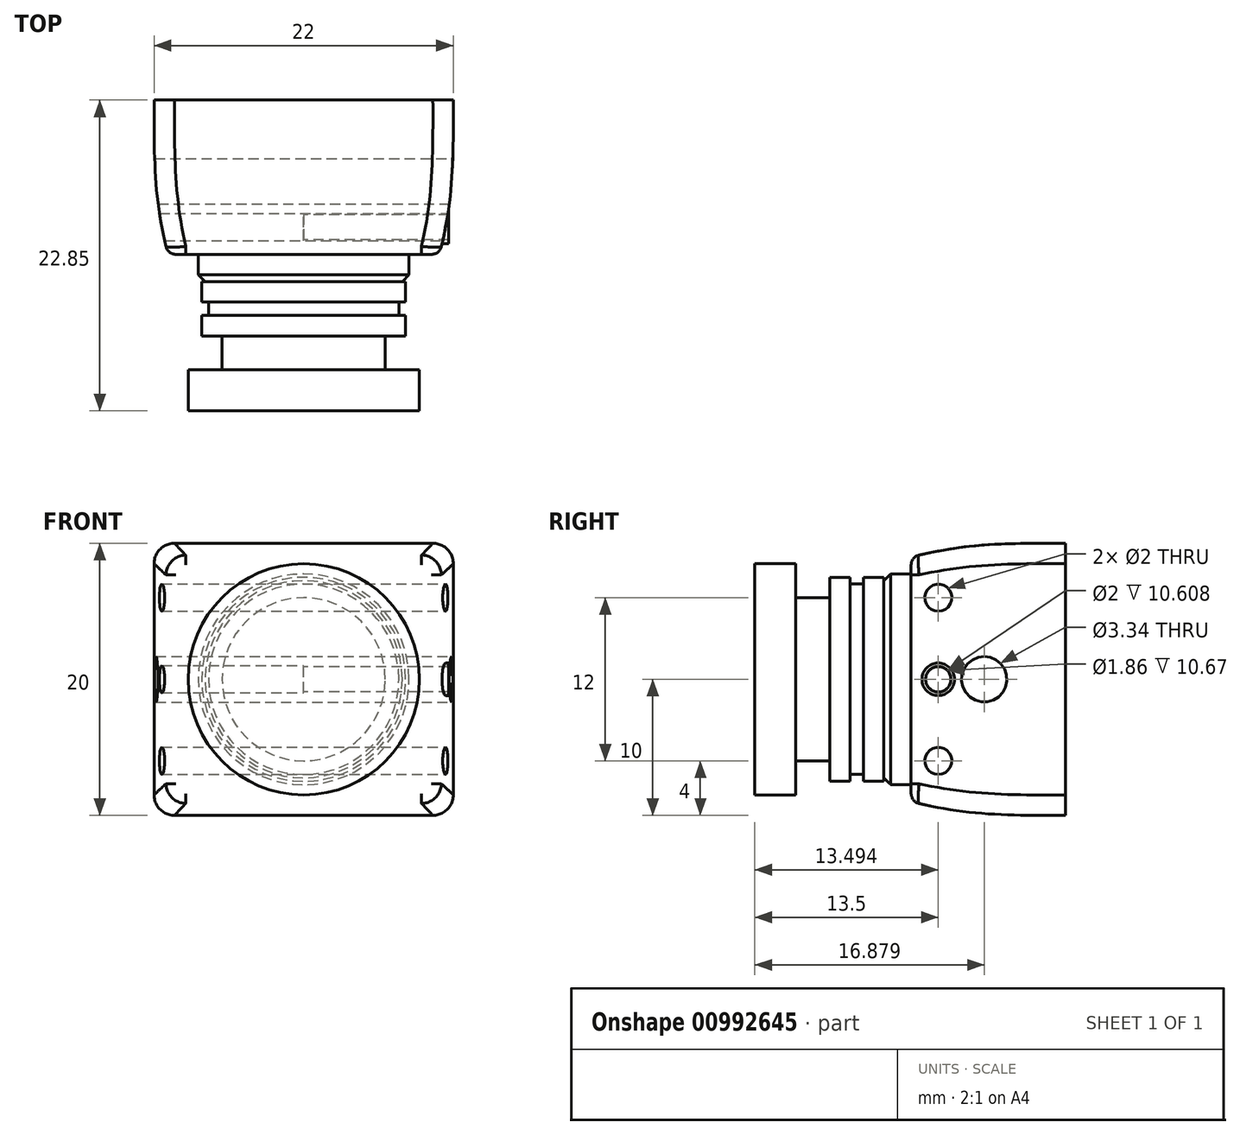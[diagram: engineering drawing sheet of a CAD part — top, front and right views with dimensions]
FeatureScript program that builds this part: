
annotation { "Feature Type Name" : "Feature", "Feature Type Description" : "" }
export const myFeature = defineFeature(function(context is Context, id is Id, definition is map)
    precondition{}
    {
        {
            var Q0;
            Q0=qCreatedBy(makeId("Front.planeOp"),FACE);
            var sketch = newSketch(context, id + "F0", { "sketchPlane" : qUnion([Q0])});
            skLineSegment(sketch, "E0.bottom", {"start": v(11, -10) * mm, "end": v(-11, -10) * mm});
            skLineSegment(sketch, "E0.top", {"start": v(11, 10) * mm, "end": v(-11, 10) * mm});
            skLineSegment(sketch, "E0.left", {"start": v(11, -10) * mm, "end": v(11, 10) * mm});
            skLineSegment(sketch, "E0.right", {"start": v(-11, -10) * mm, "end": v(-11, 10) * mm});
            skPoint(sketch, "E0.middle", {"position": v(0, 0) * mm});
            skSolve(sketch);
        }
        {
            var Q0;
            Q0=qCreatedBy(makeId("Front.planeOp"),FACE);
            cPlane(context, id + "F1", {"entities" : qUnion([Q0]), "cplaneType" : CPlaneType.OFFSET, "offset" : 11.35 * mm, "width" : 150 * mm, "height" : 150 * mm});
        }
        {
            var Q0;
            Q0=qCreatedBy(id+"F1.planeOp",FACE);
            var sketch = newSketch(context, id + "F2", { "sketchPlane" : qUnion([Q0])});
            skLineSegment(sketch, "E1.bottom", {"start": v(10, -9) * mm, "end": v(-10, -9) * mm});
            skLineSegment(sketch, "E1.top", {"start": v(10, 9) * mm, "end": v(-10, 9) * mm});
            skLineSegment(sketch, "E1.left", {"start": v(10, -9) * mm, "end": v(10, 9) * mm});
            skLineSegment(sketch, "E1.right", {"start": v(-10, -9) * mm, "end": v(-10, 9) * mm});
            skPoint(sketch, "E1.middle", {"position": v(0, 0) * mm});
            skSolve(sketch);
        }
        {
            var Q0;
            Q0=qCreatedBy(makeId("Front.planeOp"),FACE);
            cPlane(context, id + "F3", {"entities" : qUnion([Q0]), "cplaneType" : CPlaneType.OFFSET, "offset" : 9 * mm, "width" : 150 * mm, "height" : 150 * mm});
        }
        {
            var Q0;
            Q0=qCreatedBy(id+"F3.planeOp",FACE);
            var sketch = newSketch(context, id + "F4", { "sketchPlane" : qUnion([Q0])});
            skLineSegment(sketch, "E2.bottom", {"start": v(10.5, -9.5) * mm, "end": v(-10.5, -9.5) * mm});
            skLineSegment(sketch, "E2.top", {"start": v(10.5, 9.5) * mm, "end": v(-10.5, 9.5) * mm});
            skLineSegment(sketch, "E2.left", {"start": v(10.5, -9.5) * mm, "end": v(10.5, 9.5) * mm});
            skLineSegment(sketch, "E2.right", {"start": v(-10.5, -9.5) * mm, "end": v(-10.5, 9.5) * mm});
            skPoint(sketch, "E2.middle", {"position": v(0, 0) * mm});
            skSolve(sketch);
        }
        {
            var Q0;
            Q0=qSketchRegion(id+"F0",true);
            var Q1;
            Q1=qSketchRegion(id+"F4",true);
            var Q2;
            Q2=qSketchRegion(id+"F2",true);
            loft(context, id + "F5", {"sheetProfilesArray" : [{ "sheetProfileEntities" : qUnion([Q0]) }, { "sheetProfileEntities" : qUnion([Q1]) }, { "sheetProfileEntities" : qUnion([Q2]) }]});
        }
        {
            var Q0;
            Q0=makeQuery(id+"F5.opLoft","SWEPT_EDGE",EDGE,{"disambiguationData":[OSD([sQuery(id+"F0.wireOp",EDGE,"E0.top"),sQuery(id+"F0.wireOp",EDGE,"E0.left"),sQuery(id+"F2.wireOp",EDGE,"E1.top"),sQuery(id+"F2.wireOp",EDGE,"E1.left"),sQuery(id+"F4.wireOp",EDGE,"E2.top"),sQuery(id+"F4.wireOp",EDGE,"E2.left")])]});
            var Q1;
            Q1=makeQuery(id+"F5.opLoft","SWEPT_EDGE",EDGE,{"disambiguationData":[OSD([sQuery(id+"F0.wireOp",EDGE,"E0.top"),sQuery(id+"F0.wireOp",EDGE,"E0.right"),sQuery(id+"F2.wireOp",EDGE,"E1.top"),sQuery(id+"F2.wireOp",EDGE,"E1.right"),sQuery(id+"F4.wireOp",EDGE,"E2.top"),sQuery(id+"F4.wireOp",EDGE,"E2.right")])]});
            var Q2;
            Q2=makeQuery(id+"F5.opLoft","SWEPT_EDGE",EDGE,{"disambiguationData":[OSD([sQuery(id+"F0.wireOp",EDGE,"E0.bottom"),sQuery(id+"F0.wireOp",EDGE,"E0.right"),sQuery(id+"F2.wireOp",EDGE,"E1.bottom"),sQuery(id+"F2.wireOp",EDGE,"E1.right"),sQuery(id+"F4.wireOp",EDGE,"E2.bottom"),sQuery(id+"F4.wireOp",EDGE,"E2.right")])]});
            var Q3;
            Q3=makeQuery(id+"F5.opLoft","SWEPT_EDGE",EDGE,{"disambiguationData":[OSD([sQuery(id+"F0.wireOp",EDGE,"E0.bottom"),sQuery(id+"F0.wireOp",EDGE,"E0.left"),sQuery(id+"F2.wireOp",EDGE,"E1.bottom"),sQuery(id+"F2.wireOp",EDGE,"E1.left"),sQuery(id+"F4.wireOp",EDGE,"E2.bottom"),sQuery(id+"F4.wireOp",EDGE,"E2.left")])]});
            fillet(context, id + "F6", {"entities" : qUnion([Q0, Q1, Q2, Q3]), "radius" : 1.5 * mm, "tangentPropagation" : true, "allowEdgeOverflow" : false});
        }
        {
            var Q0;
            Q0=makeQuery(id+"F5.opLoft","MID_CAP_EDGE",EDGE,{"disambiguationData":[OSD([sQuery(id+"F2.wireOp",EDGE,"E1.top"),sQuery(id+"F2.wireOp",EDGE,"E1.left"),sQuery(id+"F2.wireOp",EDGE,"E1.right")])],"capPos":2.0});
            fillet(context, id + "F7", {"entities" : qUnion([Q0]), "radius" : 0.75 * mm, "tangentPropagation" : true, "allowEdgeOverflow" : false});
        }
        {
            var Q0;
            Q0=makeQuery(id+"F5.opLoft","CAP_FACE",FACE,{"disambiguationData":[OSD([makeQuery(id+"F2.imprint","IMPRINT",FACE,{"disambiguationData":[TD([[makeQuery(id+"F2.imprint","IMPRINT",EDGE,{"derivedFrom":sQuery(id+"F2.wireOp",EDGE,"E1.bottom")}),-1.0]])]})])],"isStart":true});
            var sketch = newSketch(context, id + "F8", { "sketchPlane" : qUnion([Q0])});
            skCircle(sketch, "E3", {"center": v(0, 0) * mm, "radius": 7.75 * mm});
            skSolve(sketch);
        }
        {
            var Q0;
            Q0=qSketchRegion(id+"F8",true);
            extrude(context, id + "F9", {"entities" : qUnion([Q0]), "operationType" : NewBodyOperationType.ADD, "depth" : 2 * mm, "offsetDistance" : 25 * mm});
        }
        {
            var Q0;
            Q0=makeQuery(id+"F9.opExtrude","CAP_EDGE",EDGE,{"disambiguationData":[OSD([sQuery(id+"F8.wireOp",EDGE,"E3")])],"isStart":false});
            chamfer(context, id + "F10", {"entities" : qUnion([Q0]), "width" : 0.5 * mm, "tangentPropagation" : true});
        }
        {
            var Q0;
            Q0=makeQuery(id+"F9.opExtrude","CAP_FACE",FACE,{"disambiguationData":[OSD([sQuery(id+"F8.wireOp",EDGE,"E3")])],"isStart":false});
            var sketch = newSketch(context, id + "F11", { "sketchPlane" : qUnion([Q0])});
            skCircle(sketch, "E4", {"center": v(0, 0) * mm, "radius": 7.5 * mm});
            skSolve(sketch);
        }
        {
            var Q0;
            Q0=qSketchRegion(id+"F11",true);
            extrude(context, id + "F12", {"entities" : qUnion([Q0]), "depth" : 1.5 * mm, "offsetDistance" : 25 * mm});
        }
        {
            var Q0;
            Q0=makeQuery(id+"F12.opExtrude","CAP_FACE",FACE,{"disambiguationData":[OSD([sQuery(id+"F11.wireOp",EDGE,"E4")])],"isStart":false});
            var sketch = newSketch(context, id + "F13", { "sketchPlane" : qUnion([Q0])});
            skCircle(sketch, "E5", {"center": v(0, 0) * mm, "radius": 7 * mm});
            skSolve(sketch);
        }
        {
            var Q0;
            Q0=qSketchRegion(id+"F13",true);
            extrude(context, id + "F14", {"entities" : qUnion([Q0]), "operationType" : NewBodyOperationType.ADD, "depth" : 1 * mm, "offsetDistance" : 25 * mm});
        }
        {
            var Q0;
            Q0=makeQuery(id+"F14.opExtrude","CAP_FACE",FACE,{"disambiguationData":[OSD([sQuery(id+"F13.wireOp",EDGE,"E5")])],"isStart":false});
            var sketch = newSketch(context, id + "F15", { "sketchPlane" : qUnion([Q0])});
            skCircle(sketch, "E6", {"center": v(0, 0) * mm, "radius": 7.5 * mm});
            skSolve(sketch);
        }
        {
            var Q0;
            Q0=qSketchRegion(id+"F15",true);
            extrude(context, id + "F16", {"entities" : qUnion([Q0]), "operationType" : NewBodyOperationType.ADD, "depth" : 1.5 * mm, "offsetDistance" : 25 * mm});
        }
        {
            var Q0;
            Q0=makeQuery(id+"F16.opExtrude","CAP_FACE",FACE,{"disambiguationData":[OSD([sQuery(id+"F15.wireOp",EDGE,"E6")])],"isStart":false});
            var sketch = newSketch(context, id + "F17", { "sketchPlane" : qUnion([Q0])});
            skCircle(sketch, "E7", {"center": v(0, 0) * mm, "radius": 6 * mm});
            skSolve(sketch);
        }
        {
            var Q0;
            Q0=qSketchRegion(id+"F17",true);
            extrude(context, id + "F18", {"entities" : qUnion([Q0]), "operationType" : NewBodyOperationType.ADD, "depth" : 2.5 * mm, "offsetDistance" : 25 * mm});
        }
        {
            var Q0;
            Q0=makeQuery(id+"F18.opExtrude","CAP_FACE",FACE,{"disambiguationData":[OSD([sQuery(id+"F17.wireOp",EDGE,"E7")])],"isStart":false});
            var sketch = newSketch(context, id + "F19", { "sketchPlane" : qUnion([Q0])});
            skCircle(sketch, "E8", {"center": v(0, 0) * mm, "radius": 8.5 * mm});
            skSolve(sketch);
        }
        {
            var Q0;
            Q0=qSketchRegion(id+"F19",true);
            extrude(context, id + "F20", {"entities" : qUnion([Q0]), "operationType" : NewBodyOperationType.ADD, "depth" : 3 * mm, "offsetDistance" : 25 * mm});
        }
        {
            var Q0;
            Q0=qCreatedBy(makeId("Right.planeOp"),FACE);
            var sketch = newSketch(context, id + "F21", { "sketchPlane" : qUnion([Q0])});
            skCircle(sketch, "E9", {"center": v(-5.97, 0) * mm, "radius": 1.67 * mm});
            skSolve(sketch);
        }
        {
            var Q0;
            Q0=qSketchRegion(id+"F21",true);
            extrude(context, id + "F22", {"entities" : qUnion([Q0]), "operationType" : NewBodyOperationType.ADD, "endBound" : BoundingType.SYMMETRIC, "depth" : 24.4 * mm, "offsetDistance" : 25 * mm});
        }
        {
            var Q0;
            Q0=makeQuery(id+"F22.opExtrude","CAP_FACE",FACE,{"disambiguationData":[OSD([sQuery(id+"F21.wireOp",EDGE,"E9")])],"isStart":false});
            extrude(context, id + "F23", {"entities" : qUnion([Q0]), "operationType" : NewBodyOperationType.REMOVE, "oppositeDirection" : true, "depth" : 25 * mm, "offsetDistance" : 25 * mm});
        }
        {
            var Q0;
            Q0=qCreatedBy(makeId("Right.planeOp"),FACE);
            var sketch = newSketch(context, id + "F24", { "sketchPlane" : qUnion([Q0])});
            skCircle(sketch, "E10", {"center": v(-9.35, 0) * mm, "radius": 1 * mm});
            skCircle(sketch, "E11", {"center": v(-9.35, 6) * mm, "radius": 1 * mm});
            skCircle(sketch, "E12", {"center": v(-9.35, -6) * mm, "radius": 1 * mm});
            skSolve(sketch);
        }
        {
            var Q0;
            Q0 = qSketchRegion(id + "F24", true);
            extrude(context, id + "F25", {"entities" : qUnion([Q0]), "operationType" : NewBodyOperationType.REMOVE, "endBound" : BoundingType.SYMMETRIC, "oppositeDirection" : true, "depth" : 57.8 * mm, "offsetDistance" : 25 * mm});
        }
        {
            var Q0;
            Q0=qCreatedBy(makeId("Right.planeOp"),FACE);
            var sketch = newSketch(context, id + "F26", { "sketchPlane" : qUnion([Q0])});
            skCircle(sketch, "E13", {"center": v(-9.36, 0) * mm, "radius": 1.2 * mm});
            skCircle(sketch, "E14", {"center": v(-9.36, 0) * mm, "radius": 0.93 * mm});
            skSolve(sketch);
        }
        {
            var Q0;
            Q0 = qSketchRegion(id + "F26", true);
            extrude(context, id + "F27", {"entities" : qUnion([Q0]), "operationType" : NewBodyOperationType.ADD, "depth" : 10.67 * mm, "offsetDistance" : 25 * mm});
        }
    });
